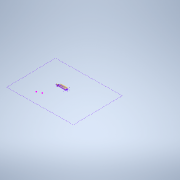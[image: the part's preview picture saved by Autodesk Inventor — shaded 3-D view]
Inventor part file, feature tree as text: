
AUTODESK INVENTOR PART (.ipt)
format: ipt  version: 2022 (Build 260153000, 153)  size: 664,576 bytes
history: native  units: mm
features: other x4, extrude x2, sketch x2
ambient origin geometry x8: Origin, YZ Plane, XZ Plane, XY Plane, X Axis, Y Axis, Z Axis, Center Point
bodies: Body1 (feature_tree)
feature tree (8):
  other  "Твердое тело1"
  other  "РабПлоскость1"
  extrude  "Выдавливание1"  Depth=25.0mm TaperAngle=0.0deg
  other  "РабПлоскость2"
  extrude  "Выдавливание3"  TaperAngle=0.0deg  [1 undecoded]
  sketch  "Эскиз1"
  sketch  "Эскиз3"
  other  "Картинка1"
note: 1 required parameter value undecoded (feature->parameter linkage not recoverable at this tier; creation-order binding heuristic only, values carry confidence <= 0.55)
